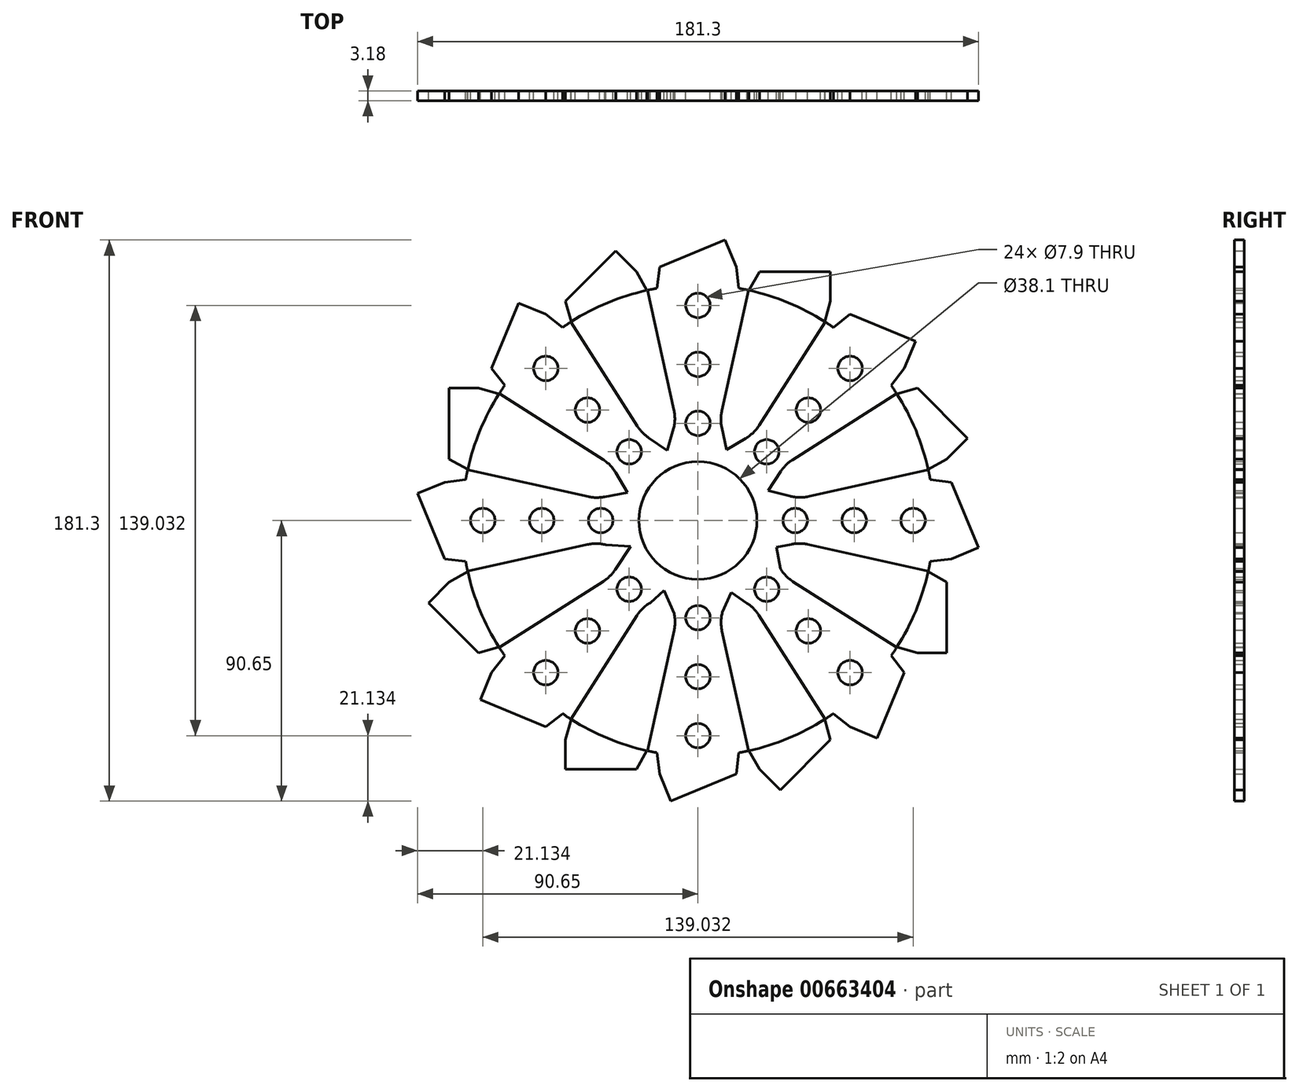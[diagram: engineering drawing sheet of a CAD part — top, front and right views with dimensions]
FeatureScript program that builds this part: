
annotation { "Feature Type Name" : "Feature", "Feature Type Description" : "" }
export const myFeature = defineFeature(function(context is Context, id is Id, definition is map)
    precondition{}
    {
        {
            var Q0;
            Q0=qCreatedBy(makeId("Front.planeOp"),FACE);
            var sketch = newSketch(context, id + "F0", { "sketchPlane" : qUnion([Q0])});
            skCircle(sketch, "E0", {"center": v(0, 0) * mm, "radius": 76.2 * mm});
            skCircle(sketch, "E1", {"center": v(0, 0) * mm, "radius": 19.05 * mm});
            skLineSegment(sketch, "E2", {"start": v(7.72, 35.47) * mm, "end": v(16.36, 74.42) * mm});
            skLineSegment(sketch, "E3.MirrorCS", {"start": v(-7.76, 35.67) * mm, "end": v(-16.36, 74.42) * mm});
            skPoint(sketch, "E4.newPointA", {"position": v(0.15, 0.03) * mm});
            skPoint(sketch, "E4.newPointB", {"position": v(-7.52, 31.44) * mm});
            skArc(sketch, "E4.filletArc", {"start": v(-7.86, 29.74) * mm, "mid": v(-7.46, 32.7) * mm, "end": v(-7.76, 35.67) * mm});
            skPoint(sketch, "E5.newPointA", {"position": v(-0.15, 0.03) * mm});
            skPoint(sketch, "E5.newPointB", {"position": v(7.52, 31.44) * mm});
            skArc(sketch, "E5.filletArc", {"start": v(7.72, 35.47) * mm, "mid": v(7.42, 32.8) * mm, "end": v(7.68, 30.13) * mm});
            skLineSegment(sketch, "E6.1.0", {"start": v(-30.71, 19.74) * mm, "end": v(-64.2, 41.06) * mm});
            skLineSegment(sketch, "E6.1.2", {"start": v(-19.63, 30.54) * mm, "end": v(-41.06, 64.2) * mm});
            skArc(sketch, "E6.1.3", {"start": v(-19.63, 30.54) * mm, "mid": v(-17.95, 28.44) * mm, "end": v(-15.87, 26.74) * mm});
            skLineSegment(sketch, "E6.1.4", {"start": v(-15.87, 26.74) * mm, "end": v(-3.93, 18.46) * mm});
            skArc(sketch, "E6.1.5", {"start": v(-26.59, 15.47) * mm, "mid": v(-28.4, 17.85) * mm, "end": v(-30.71, 19.74) * mm});
            skLineSegment(sketch, "E6.2.0", {"start": v(-35.67, -7.76) * mm, "end": v(-74.42, -16.36) * mm});
            skLineSegment(sketch, "E6.2.1", {"start": v(-29.74, -7.86) * mm, "end": v(-16.96, -8.68) * mm});
            skLineSegment(sketch, "E6.2.2", {"start": v(-35.47, 7.72) * mm, "end": v(-74.42, 16.36) * mm});
            skArc(sketch, "E6.2.3", {"start": v(-35.47, 7.72) * mm, "mid": v(-32.8, 7.42) * mm, "end": v(-30.13, 7.68) * mm});
            skLineSegment(sketch, "E6.2.4", {"start": v(-30.13, 7.68) * mm, "end": v(-15.83, 10.28) * mm});
            skArc(sketch, "E6.2.5", {"start": v(-29.74, -7.86) * mm, "mid": v(-32.7, -7.46) * mm, "end": v(-35.67, -7.76) * mm});
            skLineSegment(sketch, "E6.3.0", {"start": v(-19.74, -30.71) * mm, "end": v(-41.06, -64.2) * mm});
            skLineSegment(sketch, "E6.3.1", {"start": v(-15.47, -26.59) * mm, "end": v(-5.86, -18.13) * mm});
            skLineSegment(sketch, "E6.3.2", {"start": v(-30.54, -19.63) * mm, "end": v(-64.2, -41.06) * mm});
            skArc(sketch, "E6.3.3", {"start": v(-30.54, -19.63) * mm, "mid": v(-28.44, -17.95) * mm, "end": v(-26.74, -15.87) * mm});
            skArc(sketch, "E6.3.5", {"start": v(-15.47, -26.59) * mm, "mid": v(-17.85, -28.4) * mm, "end": v(-19.74, -30.71) * mm});
            skLineSegment(sketch, "E6.4.0", {"start": v(7.76, -35.67) * mm, "end": v(16.36, -74.42) * mm});
            skLineSegment(sketch, "E6.4.2", {"start": v(-7.72, -35.47) * mm, "end": v(-16.36, -74.42) * mm});
            skArc(sketch, "E6.4.3", {"start": v(-7.72, -35.47) * mm, "mid": v(-7.42, -32.8) * mm, "end": v(-7.68, -30.13) * mm});
            skArc(sketch, "E6.4.5", {"start": v(7.86, -29.74) * mm, "mid": v(7.46, -32.7) * mm, "end": v(7.76, -35.67) * mm});
            skLineSegment(sketch, "E6.5.0", {"start": v(30.71, -19.74) * mm, "end": v(64.2, -41.06) * mm});
            skLineSegment(sketch, "E6.5.2", {"start": v(19.63, -30.54) * mm, "end": v(41.06, -64.2) * mm});
            skArc(sketch, "E6.5.3", {"start": v(19.63, -30.54) * mm, "mid": v(17.95, -28.44) * mm, "end": v(15.87, -26.74) * mm});
            skLineSegment(sketch, "E6.5.4", {"start": v(15.87, -26.74) * mm, "end": v(3.93, -18.46) * mm});
            skArc(sketch, "E6.5.5", {"start": v(26.59, -15.47) * mm, "mid": v(28.4, -17.85) * mm, "end": v(30.71, -19.74) * mm});
            skLineSegment(sketch, "E6.6.0", {"start": v(35.67, 7.76) * mm, "end": v(74.42, 16.36) * mm});
            skLineSegment(sketch, "E6.6.2", {"start": v(35.47, -7.72) * mm, "end": v(74.42, -16.36) * mm});
            skArc(sketch, "E6.6.3", {"start": v(35.47, -7.72) * mm, "mid": v(32.8, -7.42) * mm, "end": v(30.13, -7.68) * mm});
            skArc(sketch, "E6.6.5", {"start": v(29.74, 7.86) * mm, "mid": v(32.7, 7.46) * mm, "end": v(35.67, 7.76) * mm});
            skLineSegment(sketch, "E6.7.0", {"start": v(19.74, 30.71) * mm, "end": v(41.06, 64.2) * mm});
            skLineSegment(sketch, "E6.7.2", {"start": v(30.54, 19.63) * mm, "end": v(64.2, 41.06) * mm});
            skArc(sketch, "E6.7.3", {"start": v(30.54, 19.63) * mm, "mid": v(28.44, 17.95) * mm, "end": v(26.74, 15.87) * mm});
            skArc(sketch, "E6.7.5", {"start": v(15.47, 26.59) * mm, "mid": v(17.85, 28.4) * mm, "end": v(19.74, 30.71) * mm});
            skLineSegment(sketch, "E7", {"start": v(-26.74, -15.87) * mm, "end": v(-21.82, -8.37) * mm});
            skLineSegment(sketch, "E8", {"start": v(-26.59, 15.47) * mm, "end": v(-22.79, 9.02) * mm});
            skPoint(sketch, "E9.endSnap0", {"position": v(-9.9, 22.6) * mm});
            skLineSegment(sketch, "E10", {"start": v(-9.9, 22.6) * mm, "end": v(-7.86, 29.74) * mm});
            skLineSegment(sketch, "E11", {"start": v(-7.68, -30.13) * mm, "end": v(-10.95, -22.6) * mm});
            skLineSegment(sketch, "E12", {"start": v(7.86, -29.74) * mm, "end": v(10.72, -23.17) * mm});
            skLineSegment(sketch, "E13", {"start": v(30.13, -7.68) * mm, "end": v(25.37, -8.68) * mm});
            skPoint(sketch, "E14.endSnap0", {"position": v(27.75, -8.18) * mm});
            skLineSegment(sketch, "E15", {"start": v(29.74, 7.86) * mm, "end": v(15.07, 11.66) * mm});
            skLineSegment(sketch, "E16", {"start": v(26.74, 15.87) * mm, "end": v(22.69, 9.69) * mm});
            skLineSegment(sketch, "E17", {"start": v(15.47, 26.59) * mm, "end": v(3.65, 19.63) * mm});
            skLineSegment(sketch, "E18", {"start": v(7.68, 30.13) * mm, "end": v(9.2, 22.9) * mm});
            skCircle(sketch, "E19", {"center": v(-69.52, 0) * mm, "radius": 3.95 * mm});
            skCircle(sketch, "E20.1.0.0", {"center": v(-50.47, 0) * mm, "radius": 3.95 * mm});
            skCircle(sketch, "E20.2.0.0", {"center": v(-31.42, 0) * mm, "radius": 3.95 * mm});
            skLineSegment(sketch, "E20.direction1", {"start": v(-69.52, 0) * mm, "end": v(-50.47, 0) * mm, "construction": true});
            skCircle(sketch, "E21.MirrorC", {"center": v(31.42, 0) * mm, "radius": 3.95 * mm});
            skCircle(sketch, "E22.MirrorC", {"center": v(50.47, 0) * mm, "radius": 3.95 * mm});
            skCircle(sketch, "E23.MirrorC", {"center": v(69.52, 0) * mm, "radius": 3.95 * mm});
            skLineSegment(sketch, "E24", {"start": v(-81.89, -12.39) * mm, "end": v(-75.05, -13.22) * mm});
            skLineSegment(sketch, "E25", {"start": v(-81.89, 12.39) * mm, "end": v(-75.05, 13.22) * mm});
            skLineSegment(sketch, "E26.1.0", {"start": v(-70.91, -42.78) * mm, "end": v(-64.28, -40.93) * mm});
            skLineSegment(sketch, "E26.1.1", {"start": v(-80.4, -19.89) * mm, "end": v(-74.4, -16.5) * mm});
            skLineSegment(sketch, "E26.2.0", {"start": v(-49.14, -66.66) * mm, "end": v(-43.72, -62.4) * mm});
            skLineSegment(sketch, "E26.2.1", {"start": v(-66.66, -49.14) * mm, "end": v(-62.4, -43.72) * mm});
            skLineSegment(sketch, "E26.3.0", {"start": v(-19.89, -80.4) * mm, "end": v(-16.5, -74.4) * mm});
            skLineSegment(sketch, "E26.3.1", {"start": v(-42.78, -70.91) * mm, "end": v(-40.93, -64.28) * mm});
            skLineSegment(sketch, "E26.4.0", {"start": v(12.39, -81.89) * mm, "end": v(13.22, -75.05) * mm});
            skLineSegment(sketch, "E26.4.1", {"start": v(-12.39, -81.89) * mm, "end": v(-13.22, -75.05) * mm});
            skLineSegment(sketch, "E26.5.0", {"start": v(42.78, -70.91) * mm, "end": v(40.93, -64.28) * mm});
            skLineSegment(sketch, "E26.5.1", {"start": v(19.89, -80.4) * mm, "end": v(16.5, -74.4) * mm});
            skLineSegment(sketch, "E26.6.0", {"start": v(66.66, -49.14) * mm, "end": v(62.4, -43.72) * mm});
            skLineSegment(sketch, "E26.6.1", {"start": v(49.14, -66.66) * mm, "end": v(43.72, -62.4) * mm});
            skLineSegment(sketch, "E26.7.0", {"start": v(80.4, -19.89) * mm, "end": v(74.4, -16.5) * mm});
            skLineSegment(sketch, "E26.7.1", {"start": v(70.91, -42.78) * mm, "end": v(64.28, -40.93) * mm});
            skLineSegment(sketch, "E26.8.0", {"start": v(81.89, 12.39) * mm, "end": v(75.05, 13.22) * mm});
            skLineSegment(sketch, "E26.8.1", {"start": v(81.89, -12.39) * mm, "end": v(75.05, -13.22) * mm});
            skLineSegment(sketch, "E26.9.0", {"start": v(70.91, 42.78) * mm, "end": v(64.28, 40.93) * mm});
            skLineSegment(sketch, "E26.9.1", {"start": v(80.4, 19.89) * mm, "end": v(74.4, 16.5) * mm});
            skLineSegment(sketch, "E26.10.0", {"start": v(49.14, 66.66) * mm, "end": v(43.72, 62.4) * mm});
            skLineSegment(sketch, "E26.10.1", {"start": v(66.66, 49.14) * mm, "end": v(62.4, 43.72) * mm});
            skLineSegment(sketch, "E26.11.0", {"start": v(19.89, 80.4) * mm, "end": v(16.5, 74.4) * mm});
            skLineSegment(sketch, "E26.11.1", {"start": v(42.78, 70.91) * mm, "end": v(40.93, 64.28) * mm});
            skLineSegment(sketch, "E26.12.0", {"start": v(-12.39, 81.89) * mm, "end": v(-13.22, 75.05) * mm});
            skLineSegment(sketch, "E26.12.1", {"start": v(12.39, 81.89) * mm, "end": v(13.22, 75.05) * mm});
            skLineSegment(sketch, "E26.13.0", {"start": v(-42.78, 70.91) * mm, "end": v(-40.93, 64.28) * mm});
            skLineSegment(sketch, "E26.13.1", {"start": v(-19.89, 80.4) * mm, "end": v(-16.5, 74.4) * mm});
            skLineSegment(sketch, "E26.14.0", {"start": v(-66.66, 49.14) * mm, "end": v(-62.4, 43.72) * mm});
            skLineSegment(sketch, "E26.14.1", {"start": v(-49.14, 66.66) * mm, "end": v(-43.72, 62.4) * mm});
            skLineSegment(sketch, "E26.15.0", {"start": v(-80.4, 19.89) * mm, "end": v(-74.4, 16.5) * mm});
            skLineSegment(sketch, "E26.15.1", {"start": v(-70.91, 42.78) * mm, "end": v(-64.28, 40.93) * mm});
            skLineSegment(sketch, "E27", {"start": v(25.37, -8.68) * mm, "end": v(26.59, -15.47) * mm});
            skLineSegment(sketch, "E28", {"start": v(-80.4, 19.89) * mm, "end": v(-80.4, 42.78) * mm});
            skLineSegment(sketch, "E29", {"start": v(-80.4, 42.78) * mm, "end": v(-70.91, 42.78) * mm});
            skLineSegment(sketch, "E30.1.0", {"start": v(-81.89, -12.39) * mm, "end": v(-90.65, 8.76) * mm});
            skLineSegment(sketch, "E30.1.1", {"start": v(-90.65, 8.76) * mm, "end": v(-81.89, 12.39) * mm});
            skLineSegment(sketch, "E30.2.0", {"start": v(-70.91, -42.78) * mm, "end": v(-87.1, -26.6) * mm});
            skLineSegment(sketch, "E30.2.1", {"start": v(-87.1, -26.6) * mm, "end": v(-80.4, -19.89) * mm});
            skLineSegment(sketch, "E30.3.0", {"start": v(-49.14, -66.66) * mm, "end": v(-70.3, -57.9) * mm});
            skLineSegment(sketch, "E30.3.1", {"start": v(-70.3, -57.9) * mm, "end": v(-66.66, -49.14) * mm});
            skLineSegment(sketch, "E30.4.0", {"start": v(-19.89, -80.4) * mm, "end": v(-42.78, -80.4) * mm});
            skLineSegment(sketch, "E30.4.1", {"start": v(-42.78, -80.4) * mm, "end": v(-42.78, -70.91) * mm});
            skLineSegment(sketch, "E30.5.0", {"start": v(12.39, -81.89) * mm, "end": v(-8.76, -90.65) * mm});
            skLineSegment(sketch, "E30.5.1", {"start": v(-8.76, -90.65) * mm, "end": v(-12.39, -81.89) * mm});
            skLineSegment(sketch, "E30.6.0", {"start": v(42.78, -70.91) * mm, "end": v(26.6, -87.1) * mm});
            skLineSegment(sketch, "E30.6.1", {"start": v(26.6, -87.1) * mm, "end": v(19.89, -80.4) * mm});
            skLineSegment(sketch, "E30.7.0", {"start": v(66.66, -49.14) * mm, "end": v(57.9, -70.3) * mm});
            skLineSegment(sketch, "E30.7.1", {"start": v(57.9, -70.3) * mm, "end": v(49.14, -66.66) * mm});
            skLineSegment(sketch, "E30.8.0", {"start": v(80.4, -19.89) * mm, "end": v(80.4, -42.78) * mm});
            skLineSegment(sketch, "E30.8.1", {"start": v(80.4, -42.78) * mm, "end": v(70.91, -42.78) * mm});
            skLineSegment(sketch, "E30.9.0", {"start": v(81.89, 12.39) * mm, "end": v(90.65, -8.76) * mm});
            skLineSegment(sketch, "E30.9.1", {"start": v(90.65, -8.76) * mm, "end": v(81.89, -12.39) * mm});
            skLineSegment(sketch, "E30.10.0", {"start": v(70.91, 42.78) * mm, "end": v(87.1, 26.6) * mm});
            skLineSegment(sketch, "E30.10.1", {"start": v(87.1, 26.6) * mm, "end": v(80.4, 19.89) * mm});
            skLineSegment(sketch, "E30.11.0", {"start": v(49.14, 66.66) * mm, "end": v(70.3, 57.9) * mm});
            skLineSegment(sketch, "E30.11.1", {"start": v(70.3, 57.9) * mm, "end": v(66.66, 49.14) * mm});
            skLineSegment(sketch, "E30.12.0", {"start": v(19.89, 80.4) * mm, "end": v(42.78, 80.4) * mm});
            skLineSegment(sketch, "E30.12.1", {"start": v(42.78, 80.4) * mm, "end": v(42.78, 70.91) * mm});
            skLineSegment(sketch, "E30.13.0", {"start": v(-12.39, 81.89) * mm, "end": v(8.76, 90.65) * mm});
            skLineSegment(sketch, "E30.13.1", {"start": v(8.76, 90.65) * mm, "end": v(12.39, 81.89) * mm});
            skLineSegment(sketch, "E30.14.0", {"start": v(-42.78, 70.91) * mm, "end": v(-26.6, 87.1) * mm});
            skLineSegment(sketch, "E30.14.1", {"start": v(-26.6, 87.1) * mm, "end": v(-19.89, 80.4) * mm});
            skLineSegment(sketch, "E30.15.0", {"start": v(-66.66, 49.14) * mm, "end": v(-57.9, 70.3) * mm});
            skLineSegment(sketch, "E30.15.1", {"start": v(-57.9, 70.3) * mm, "end": v(-49.14, 66.66) * mm});
            skCircle(sketch, "E31.1.0", {"center": v(-49.16, 49.16) * mm, "radius": 3.95 * mm});
            skCircle(sketch, "E31.1.1", {"center": v(-35.69, 35.69) * mm, "radius": 3.95 * mm});
            skCircle(sketch, "E31.1.2", {"center": v(-22.21, 22.21) * mm, "radius": 3.95 * mm});
            skCircle(sketch, "E31.1.3", {"center": v(22.21, -22.21) * mm, "radius": 3.95 * mm});
            skCircle(sketch, "E31.1.4", {"center": v(35.69, -35.69) * mm, "radius": 3.95 * mm});
            skCircle(sketch, "E31.1.5", {"center": v(49.16, -49.16) * mm, "radius": 3.95 * mm});
            skCircle(sketch, "E31.2.0", {"center": v(0, 69.52) * mm, "radius": 3.95 * mm});
            skCircle(sketch, "E31.2.1", {"center": v(0, 50.47) * mm, "radius": 3.95 * mm});
            skCircle(sketch, "E31.2.2", {"center": v(0, 31.42) * mm, "radius": 3.95 * mm});
            skCircle(sketch, "E31.2.3", {"center": v(0, -31.42) * mm, "radius": 3.95 * mm});
            skCircle(sketch, "E31.2.4", {"center": v(0, -50.47) * mm, "radius": 3.95 * mm});
            skCircle(sketch, "E31.2.5", {"center": v(0, -69.52) * mm, "radius": 3.95 * mm});
            skLineSegment(sketch, "E31.anchor1", {"start": v(0, 0) * mm, "end": v(-69.52, 0) * mm, "construction": true});
            skLineSegment(sketch, "E31.anchor2", {"start": v(0, 0) * mm, "end": v(0, 69.52) * mm, "construction": true});
            skCircle(sketch, "E32.MirrorC", {"center": v(22.21, 22.21) * mm, "radius": 3.95 * mm});
            skCircle(sketch, "E33.MirrorC", {"center": v(35.69, 35.69) * mm, "radius": 3.95 * mm});
            skCircle(sketch, "E34.MirrorC", {"center": v(49.16, 49.16) * mm, "radius": 3.95 * mm});
            skCircle(sketch, "E35.MirrorC", {"center": v(-22.21, -22.21) * mm, "radius": 3.95 * mm});
            skCircle(sketch, "E36.MirrorC", {"center": v(-49.16, -49.16) * mm, "radius": 3.95 * mm});
            skCircle(sketch, "E37.MirrorC", {"center": v(-35.69, -35.69) * mm, "radius": 3.95 * mm});
            skSolve(sketch);
        }
        {
            var Q0;
            Q0=makeQuery(id+"F0.imprint","IMPRINT",FACE,{"disambiguationData":[TD([[makeQuery(id+"F0.imprint","IMPRINT",EDGE,{"derivedFrom":sQuery(id+"F0.wireOp",EDGE,"95afa0ed-20f6-4af9-8ee1-7066b4bdbd98.13.1")}),1.0]])]});
            var Q1;
            Q1=makeQuery(id+"F0.imprint","IMPRINT",FACE,{"disambiguationData":[TD([[makeQuery(id+"F0.imprint","IMPRINT",EDGE,{"derivedFrom":sQuery(id+"F0.wireOp",EDGE,"95afa0ed-20f6-4af9-8ee1-7066b4bdbd98.14.1")}),1.0]])]});
            var Q2;
            Q2=makeQuery(id+"F0.imprint","IMPRINT",FACE,{"disambiguationData":[TD([[makeQuery(id+"F0.imprint","IMPRINT",EDGE,{"derivedFrom":sQuery(id+"F0.wireOp",EDGE,"95afa0ed-20f6-4af9-8ee1-7066b4bdbd98.15.1")}),1.0]])]});
            var Q3;
            Q3=makeQuery(id+"F0.imprint","IMPRINT",FACE,{"disambiguationData":[TD([[makeQuery(id+"F0.imprint","IMPRINT",EDGE,{"derivedFrom":sQuery(id+"F0.wireOp",EDGE,"oBpBuFJF-Vkpq-FJom-suPy-hN6SrBEoH00M")}),1.0]])]});
            var Q4;
            Q4=makeQuery(id+"F0.imprint","IMPRINT",FACE,{"disambiguationData":[TD([[makeQuery(id+"F0.imprint","IMPRINT",EDGE,{"derivedFrom":sQuery(id+"F0.wireOp",EDGE,"95afa0ed-20f6-4af9-8ee1-7066b4bdbd98.1.1")}),1.0]])]});
            var Q5;
            Q5=makeQuery(id+"F0.imprint","IMPRINT",FACE,{"disambiguationData":[TD([[makeQuery(id+"F0.imprint","IMPRINT",EDGE,{"derivedFrom":sQuery(id+"F0.wireOp",EDGE,"95afa0ed-20f6-4af9-8ee1-7066b4bdbd98.2.1")}),1.0]])]});
            var Q6;
            Q6=makeQuery(id+"F0.imprint","IMPRINT",FACE,{"disambiguationData":[TD([[makeQuery(id+"F0.imprint","IMPRINT",EDGE,{"derivedFrom":sQuery(id+"F0.wireOp",EDGE,"95afa0ed-20f6-4af9-8ee1-7066b4bdbd98.3.1")}),1.0]])]});
            var Q7;
            Q7=makeQuery(id+"F0.imprint","IMPRINT",FACE,{"disambiguationData":[TD([[makeQuery(id+"F0.imprint","IMPRINT",EDGE,{"derivedFrom":sQuery(id+"F0.wireOp",EDGE,"95afa0ed-20f6-4af9-8ee1-7066b4bdbd98.4.1")}),1.0]])]});
            var Q8;
            Q8=makeQuery(id+"F0.imprint","IMPRINT",FACE,{"disambiguationData":[TD([[makeQuery(id+"F0.imprint","IMPRINT",EDGE,{"derivedFrom":sQuery(id+"F0.wireOp",EDGE,"95afa0ed-20f6-4af9-8ee1-7066b4bdbd98.5.1")}),1.0]])]});
            var Q9;
            Q9=makeQuery(id+"F0.imprint","IMPRINT",FACE,{"disambiguationData":[TD([[makeQuery(id+"F0.imprint","IMPRINT",EDGE,{"derivedFrom":sQuery(id+"F0.wireOp",EDGE,"95afa0ed-20f6-4af9-8ee1-7066b4bdbd98.6.1")}),1.0]])]});
            var Q10;
            Q10=makeQuery(id+"F0.imprint","IMPRINT",FACE,{"disambiguationData":[TD([[makeQuery(id+"F0.imprint","IMPRINT",EDGE,{"derivedFrom":sQuery(id+"F0.wireOp",EDGE,"95afa0ed-20f6-4af9-8ee1-7066b4bdbd98.7.1")}),1.0]])]});
            var Q11;
            Q11=makeQuery(id+"F0.imprint","IMPRINT",FACE,{"disambiguationData":[TD([[makeQuery(id+"F0.imprint","IMPRINT",EDGE,{"derivedFrom":sQuery(id+"F0.wireOp",EDGE,"95afa0ed-20f6-4af9-8ee1-7066b4bdbd98.8.1")}),1.0]])]});
            var Q12;
            Q12=makeQuery(id+"F0.imprint","IMPRINT",FACE,{"disambiguationData":[TD([[makeQuery(id+"F0.imprint","IMPRINT",EDGE,{"derivedFrom":sQuery(id+"F0.wireOp",EDGE,"95afa0ed-20f6-4af9-8ee1-7066b4bdbd98.9.1")}),1.0]])]});
            var Q13;
            Q13=makeQuery(id+"F0.imprint","IMPRINT",FACE,{"disambiguationData":[TD([[makeQuery(id+"F0.imprint","IMPRINT",EDGE,{"derivedFrom":sQuery(id+"F0.wireOp",EDGE,"95afa0ed-20f6-4af9-8ee1-7066b4bdbd98.10.1")}),1.0]])]});
            var Q14;
            Q14=makeQuery(id+"F0.imprint","IMPRINT",FACE,{"disambiguationData":[TD([[makeQuery(id+"F0.imprint","IMPRINT",EDGE,{"derivedFrom":sQuery(id+"F0.wireOp",EDGE,"95afa0ed-20f6-4af9-8ee1-7066b4bdbd98.11.1")}),1.0]])]});
            var Q15;
            Q15=makeQuery(id+"F0.imprint","IMPRINT",FACE,{"disambiguationData":[TD([[makeQuery(id+"F0.imprint","IMPRINT",EDGE,{"derivedFrom":sQuery(id+"F0.wireOp",EDGE,"95afa0ed-20f6-4af9-8ee1-7066b4bdbd98.12.1")}),1.0]])]});
            var Q16;
            {var subQ3=sQuery(id+"F0.wireOp",EDGE,"E6.1.0");Q16=makeQuery(id+"F0.imprint","IMPRINT",FACE,{"disambiguationData":[TD([[makeQuery(id+"F0.imprint","IMPRINT",EDGE,{"derivedFrom":subQ3}),-1.0]])]});}
            var Q17;
            {var subQ1=sQuery(id+"F0.wireOp",EDGE,"E2");Q17=makeQuery(id+"F0.imprint","IMPRINT",FACE,{"disambiguationData":[TD([[makeQuery(id+"F0.imprint","IMPRINT",EDGE,{"derivedFrom":subQ1}),1.0]])]});}
            var Q18;
            {var subQ4=sQuery(id+"F0.wireOp",EDGE,"E6.2.0");Q18=makeQuery(id+"F0.imprint","IMPRINT",FACE,{"disambiguationData":[TD([[makeQuery(id+"F0.imprint","IMPRINT",EDGE,{"derivedFrom":subQ4}),-1.0]])]});}
            var Q19;
            {var subQ13=sQuery(id+"F0.wireOp",EDGE,"E6.5.2");Q19=makeQuery(id+"F0.imprint","IMPRINT",FACE,{"disambiguationData":[TD([[makeQuery(id+"F0.imprint","IMPRINT",EDGE,{"derivedFrom":subQ13}),1.0]])]});}
            var Q20;
            {var subQ4=sQuery(id+"F0.wireOp",EDGE,"E6.4.0");Q20=makeQuery(id+"F0.imprint","IMPRINT",FACE,{"disambiguationData":[TD([[makeQuery(id+"F0.imprint","IMPRINT",EDGE,{"derivedFrom":subQ4}),-1.0]])]});}
            var Q21;
            {var subQ1=sQuery(id+"F0.wireOp",EDGE,"E6.3.0");Q21=makeQuery(id+"F0.imprint","IMPRINT",FACE,{"disambiguationData":[TD([[makeQuery(id+"F0.imprint","IMPRINT",EDGE,{"derivedFrom":subQ1}),-1.0]])]});}
            var Q22;
            {var subQ1=sQuery(id+"F0.wireOp",EDGE,"E24");Q22=makeQuery(id+"F0.imprint","IMPRINT",FACE,{"disambiguationData":[TD([[makeQuery(id+"F0.imprint","IMPRINT",EDGE,{"derivedFrom":subQ1}),1.0]])]});}
            var Q23;
            {var subQ1=sQuery(id+"F0.wireOp",EDGE,"E26.15.0");Q23=makeQuery(id+"F0.imprint","IMPRINT",FACE,{"disambiguationData":[TD([[makeQuery(id+"F0.imprint","IMPRINT",EDGE,{"derivedFrom":subQ1}),1.0]])]});}
            var Q24;
            {var subQ0=sQuery(id+"F0.wireOp",EDGE,"E26.14.0");Q24=makeQuery(id+"F0.imprint","IMPRINT",FACE,{"disambiguationData":[TD([[makeQuery(id+"F0.imprint","IMPRINT",EDGE,{"derivedFrom":subQ0}),1.0]])]});}
            var Q25;
            {var subQ1=sQuery(id+"F0.wireOp",EDGE,"E26.13.0");Q25=makeQuery(id+"F0.imprint","IMPRINT",FACE,{"disambiguationData":[TD([[makeQuery(id+"F0.imprint","IMPRINT",EDGE,{"derivedFrom":subQ1}),1.0]])]});}
            var Q26;
            {var subQ1=sQuery(id+"F0.wireOp",EDGE,"E26.12.0");Q26=makeQuery(id+"F0.imprint","IMPRINT",FACE,{"disambiguationData":[TD([[makeQuery(id+"F0.imprint","IMPRINT",EDGE,{"derivedFrom":subQ1}),1.0]])]});}
            var Q27;
            {var subQ1=sQuery(id+"F0.wireOp",EDGE,"E26.11.0");Q27=makeQuery(id+"F0.imprint","IMPRINT",FACE,{"disambiguationData":[TD([[makeQuery(id+"F0.imprint","IMPRINT",EDGE,{"derivedFrom":subQ1}),1.0]])]});}
            var Q28;
            {var subQ1=sQuery(id+"F0.wireOp",EDGE,"E26.10.0");Q28=makeQuery(id+"F0.imprint","IMPRINT",FACE,{"disambiguationData":[TD([[makeQuery(id+"F0.imprint","IMPRINT",EDGE,{"derivedFrom":subQ1}),1.0]])]});}
            var Q29;
            {var subQ0=sQuery(id+"F0.wireOp",EDGE,"E26.9.0");Q29=makeQuery(id+"F0.imprint","IMPRINT",FACE,{"disambiguationData":[TD([[makeQuery(id+"F0.imprint","IMPRINT",EDGE,{"derivedFrom":subQ0}),1.0]])]});}
            var Q30;
            {var subQ1=sQuery(id+"F0.wireOp",EDGE,"E26.8.0");Q30=makeQuery(id+"F0.imprint","IMPRINT",FACE,{"disambiguationData":[TD([[makeQuery(id+"F0.imprint","IMPRINT",EDGE,{"derivedFrom":subQ1}),1.0]])]});}
            var Q31;
            {var subQ1=sQuery(id+"F0.wireOp",EDGE,"E26.7.0");Q31=makeQuery(id+"F0.imprint","IMPRINT",FACE,{"disambiguationData":[TD([[makeQuery(id+"F0.imprint","IMPRINT",EDGE,{"derivedFrom":subQ1}),1.0]])]});}
            var Q32;
            {var subQ0=sQuery(id+"F0.wireOp",EDGE,"E26.6.0");Q32=makeQuery(id+"F0.imprint","IMPRINT",FACE,{"disambiguationData":[TD([[makeQuery(id+"F0.imprint","IMPRINT",EDGE,{"derivedFrom":subQ0}),1.0]])]});}
            var Q33;
            {var subQ1=sQuery(id+"F0.wireOp",EDGE,"E26.4.0");Q33=makeQuery(id+"F0.imprint","IMPRINT",FACE,{"disambiguationData":[TD([[makeQuery(id+"F0.imprint","IMPRINT",EDGE,{"derivedFrom":subQ1}),1.0]])]});}
            var Q34;
            {var subQ1=sQuery(id+"F0.wireOp",EDGE,"E26.2.0");Q34=makeQuery(id+"F0.imprint","IMPRINT",FACE,{"disambiguationData":[TD([[makeQuery(id+"F0.imprint","IMPRINT",EDGE,{"derivedFrom":subQ1}),1.0]])]});}
            var Q35;
            {var subQ0=sQuery(id+"F0.wireOp",EDGE,"E26.1.0");Q35=makeQuery(id+"F0.imprint","IMPRINT",FACE,{"disambiguationData":[TD([[makeQuery(id+"F0.imprint","IMPRINT",EDGE,{"derivedFrom":subQ0}),1.0]])]});}
            var Q36;
            {var subQ1=sQuery(id+"F0.wireOp",EDGE,"E26.5.0");Q36=makeQuery(id+"F0.imprint","IMPRINT",FACE,{"disambiguationData":[TD([[makeQuery(id+"F0.imprint","IMPRINT",EDGE,{"derivedFrom":subQ1}),1.0]])]});}
            var Q37;
            {var subQ1=sQuery(id+"F0.wireOp",EDGE,"E26.3.0");Q37=makeQuery(id+"F0.imprint","IMPRINT",FACE,{"disambiguationData":[TD([[makeQuery(id+"F0.imprint","IMPRINT",EDGE,{"derivedFrom":subQ1}),1.0]])]});}
            extrude(context, id + "F1", {"entities" : qUnion([Q0, Q1, Q2, Q3, Q4, Q5, Q6, Q7, Q8, Q9, Q10, Q11, Q12, Q13, Q14, Q15, Q16, Q17, Q18, Q19, Q20, Q21, Q22, Q23, Q24, Q25, Q26, Q27, Q28, Q29, Q30, Q31, Q32, Q33, Q34, Q35, Q36, Q37]), "depth" : 3.17 * mm, "offsetDistance" : 25.4 * mm});
        }
    });
